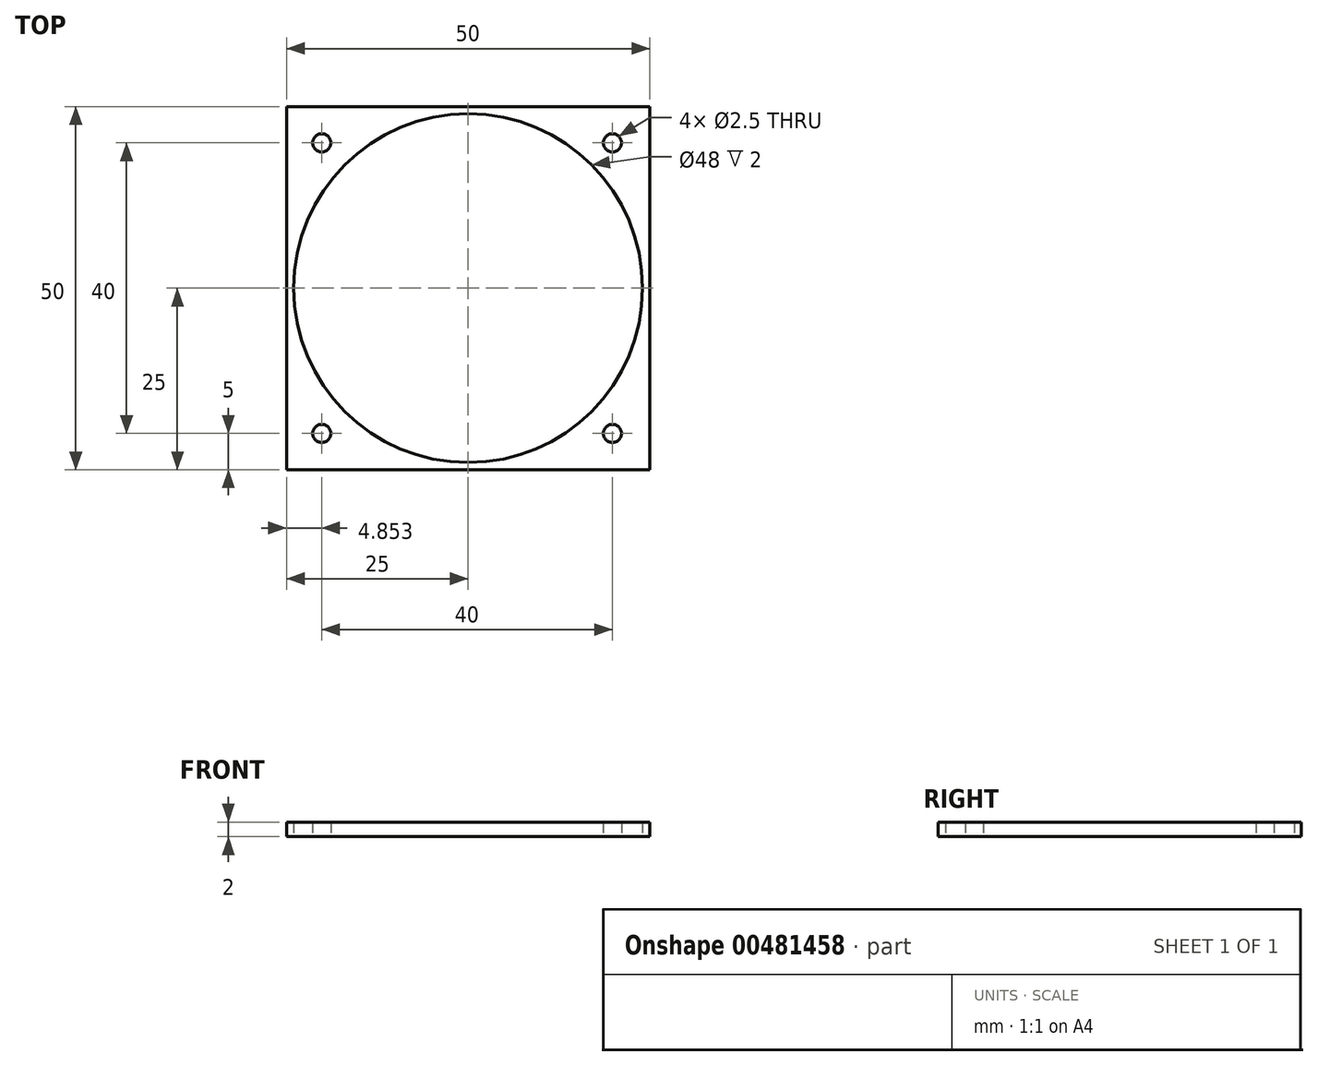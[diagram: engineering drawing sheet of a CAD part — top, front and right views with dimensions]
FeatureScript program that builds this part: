
annotation { "Feature Type Name" : "Feature", "Feature Type Description" : "" }
export const myFeature = defineFeature(function(context is Context, id is Id, definition is map)
    precondition{}
    {
        {
            var Q0;
            Q0=qCreatedBy(makeId("Top.planeOp"),FACE);
            var sketch = newSketch(context, id + "F0", { "sketchPlane" : qUnion([Q0])});
            skLineSegment(sketch, "E0.bottom", {"start": v(0, 0) * mm, "end": v(-50, 0) * mm});
            skLineSegment(sketch, "E0.top", {"start": v(0, 50) * mm, "end": v(-50, 50) * mm});
            skLineSegment(sketch, "E0.left", {"start": v(0, 0) * mm, "end": v(0, 50) * mm});
            skLineSegment(sketch, "E0.right", {"start": v(-50, 0) * mm, "end": v(-50, 50) * mm});
            skLineSegment(sketch, "E1", {"start": v(-50, 0) * mm, "end": v(0, 50) * mm, "construction": true});
            skCircle(sketch, "E2", {"center": v(-25, 25) * mm, "radius": 24 * mm});
            skCircle(sketch, "E3", {"center": v(-45.15, 45) * mm, "radius": 1.25 * mm});
            skCircle(sketch, "E4", {"center": v(-5.15, 45) * mm, "radius": 1.25 * mm});
            skLineSegment(sketch, "E5", {"start": v(-45.15, 45) * mm, "end": v(-5.15, 45) * mm, "construction": true});
            skLineSegment(sketch, "E6", {"start": v(-25, 25) * mm, "end": v(-25, 45) * mm, "construction": true});
            skPoint(sketch, "E6.endSnap0", {"position": v(-25.15, 45) * mm});
            skLineSegment(sketch, "E7", {"start": v(-25, 25) * mm, "end": v(-36.8, 25) * mm, "construction": true});
            skCircle(sketch, "E8.MirrorC", {"center": v(-45.15, 5) * mm, "radius": 1.25 * mm});
            skCircle(sketch, "E9.MirrorC", {"center": v(-5.15, 5) * mm, "radius": 1.25 * mm});
            skLineSegment(sketch, "E10", {"start": v(-5.15, 5) * mm, "end": v(-5.15, 45) * mm, "construction": true});
            skLineSegment(sketch, "E11", {"start": v(-25, 25) * mm, "end": v(-5.15, 25) * mm, "construction": true});
            skSolve(sketch);
        }
        {
            var Q0;
            Q0=makeQuery(id+"F0.imprint","IMPRINT",FACE,{"disambiguationData":[TD([[makeQuery(id+"F0.imprint","IMPRINT",EDGE,{"derivedFrom":sQuery(id+"F0.wireOp",EDGE,"E0.bottom")}),-1.0]])]});
            extrude(context, id + "F1", {"entities" : qUnion([Q0]), "depth" : 2 * mm});
        }
    });
